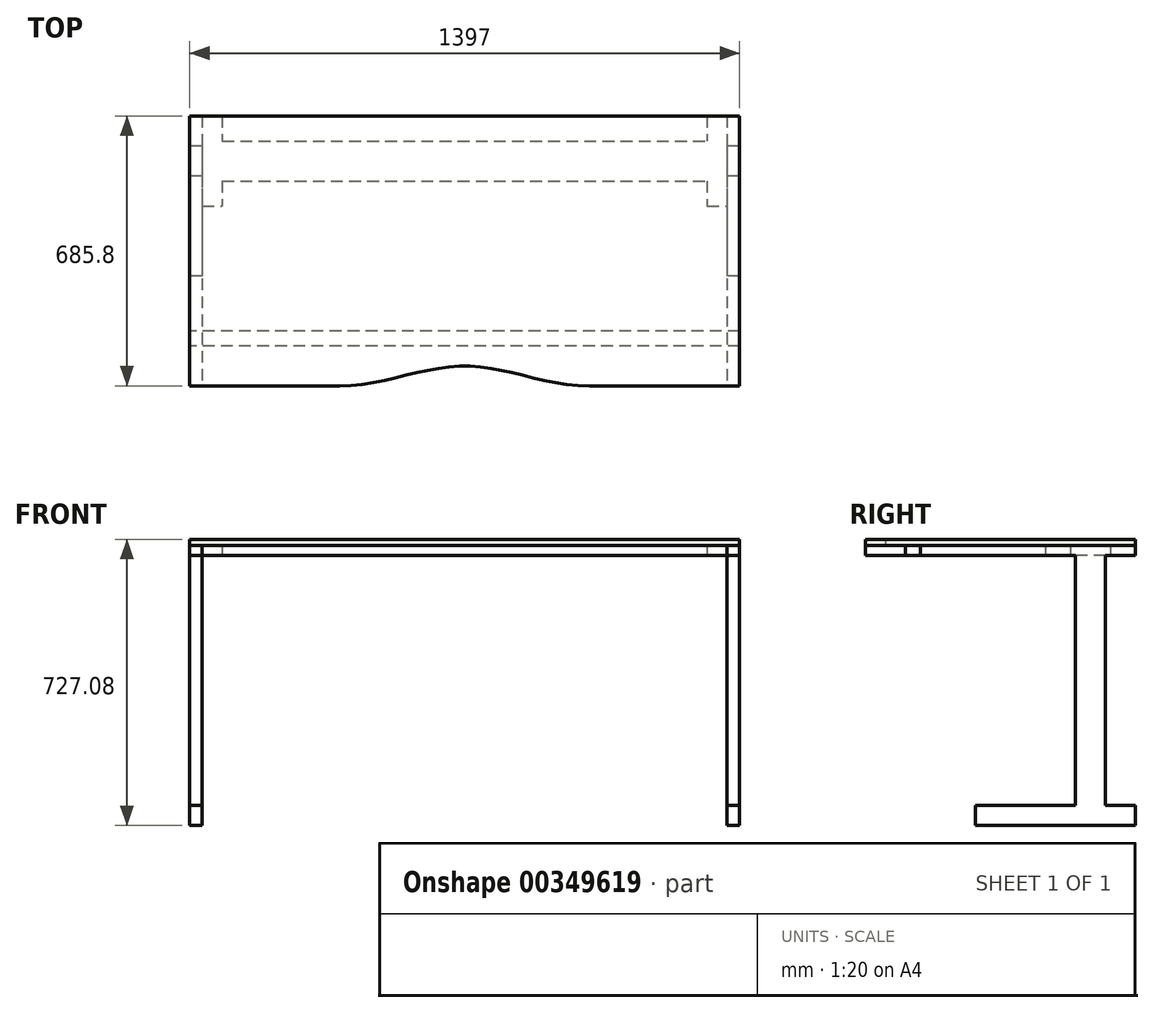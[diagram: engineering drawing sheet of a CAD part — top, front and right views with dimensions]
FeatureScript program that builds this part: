
annotation { "Feature Type Name" : "Feature", "Feature Type Description" : "" }
export const myFeature = defineFeature(function(context is Context, id is Id, definition is map)
    precondition{}
    {
        {
            var Q0;
            Q0=qCreatedBy(makeId("Top.planeOp"),FACE);
            var sketch = newSketch(context, id + "F0", { "sketchPlane" : qUnion([Q0])});
            skLineSegment(sketch, "E0.bottom", {"start": v(0, 0) * mm, "end": v(381, 0) * mm});
            skLineSegment(sketch, "E0.top", {"start": v(0, 685.8) * mm, "end": v(1397, 685.8) * mm});
            skLineSegment(sketch, "E0.left", {"start": v(0, 0) * mm, "end": v(0, 685.8) * mm});
            skLineSegment(sketch, "E0.right", {"start": v(1397, 0) * mm, "end": v(1397, 685.8) * mm});
            skPoint(sketch, "E1", {"position": v(1016, 0) * mm});
            skPoint(sketch, "E2", {"position": v(381, 0) * mm});
            skPoint(sketch, "E3", {"position": v(698.5, 50.8) * mm});
            skLineSegment(sketch, "E4.trimOffspring", {"start": v(1016, 0) * mm, "end": v(1397, 0) * mm});
            skFitSpline(sketch, "E5", {"points": [v(381, 0) * mm, v(698.5, 50.8) * mm, v(1016, 0) * mm], "startDerivative": vector(659.31, 0) * mm, "endDerivative": vector(699.63, 0) * mm});
            skSolve(sketch);
        }
        {
            var Q0;
            Q0 = qSketchRegion(id + "F0", true);
            extrude(context, id + "F1", {"entities" : qUnion([Q0]), "depth" : 15.88 * mm});
        }
        {
            var Q0;
            Q0=makeQuery(id+"F1.opExtrude","SWEPT_FACE",FACE,{"disambiguationData":[OSD([sQuery(id+"F0.wireOp",EDGE,"E0.left")])]});
            var sketch = newSketch(context, id + "F2", { "sketchPlane" : qUnion([Q0])});
            skPoint(sketch, "E6", {"position": v(-609.6, 0) * mm});
            skPoint(sketch, "E7", {"position": v(-533.4, 0) * mm});
            skLineSegment(sketch, "E8.bottom", {"start": v(-609.6, 0) * mm, "end": v(-533.4, 0) * mm});
            skLineSegment(sketch, "E8.top", {"start": v(-609.6, -711.2) * mm, "end": v(-533.4, -711.2) * mm});
            skLineSegment(sketch, "E8.left", {"start": v(-609.6, 0) * mm, "end": v(-609.6, -711.2) * mm});
            skLineSegment(sketch, "E8.right", {"start": v(-533.4, 0) * mm, "end": v(-533.4, -711.2) * mm});
            skLineSegment(sketch, "E9.bottom", {"start": v(-685.8, 0) * mm, "end": v(0, 0) * mm});
            skLineSegment(sketch, "E9.top", {"start": v(-685.8, -25.4) * mm, "end": v(0, -25.4) * mm});
            skLineSegment(sketch, "E9.left", {"start": v(-685.8, 0) * mm, "end": v(-685.8, -25.4) * mm});
            skLineSegment(sketch, "E9.right", {"start": v(0, 0) * mm, "end": v(0, -25.4) * mm});
            skSolve(sketch);
        }
        {
            var Q0;
            Q0 = qSketchRegion(id + "F2", true);
            extrude(context, id + "F3", {"entities" : qUnion([Q0]), "oppositeDirection" : true, "depth" : 1397 * mm});
        }
        {
            var Q0;
            Q0=makeQuery(id+"F3.opExtrude","SWEPT_FACE",FACE,{"disambiguationData":[OSD([sQuery(id+"F2.wireOp",EDGE,"E8.right")])]});
            var sketch = newSketch(context, id + "F4", { "sketchPlane" : qUnion([Q0])});
            skPoint(sketch, "E10", {"position": v(31.75, -711.2) * mm});
            skLineSegment(sketch, "E11.left", {"start": v(31.75, -711.2) * mm, "end": v(31.75, -711.2) * mm});
            skLineSegment(sketch, "E11.right", {"start": v(1365.25, -711.2) * mm, "end": v(1365.25, -711.2) * mm});
            skLineSegment(sketch, "E12.bottom", {"start": v(31.75, -711.2) * mm, "end": v(1365.25, -711.2) * mm});
            skLineSegment(sketch, "E12.top", {"start": v(31.75, -25.4) * mm, "end": v(1365.25, -25.4) * mm});
            skLineSegment(sketch, "E12.left", {"start": v(31.75, -711.2) * mm, "end": v(31.75, -25.4) * mm});
            skLineSegment(sketch, "E12.right", {"start": v(1365.25, -711.2) * mm, "end": v(1365.25, -25.4) * mm});
            skSolve(sketch);
        }
        {
            var Q0;
            Q0 = qSketchRegion(id + "F4", true);
            extrude(context, id + "F5", {"entities" : qUnion([Q0]), "operationType" : NewBodyOperationType.REMOVE, "oppositeDirection" : true, "depth" : 76.2 * mm});
        }
        {
            var Q0;
            Q0=makeQuery(id+"F3.boolean.opBoolean","MERGE",FACE,{"derivedFrom":[makeQuery(id+"F1.opExtrude","SWEPT_FACE",FACE,{"disambiguationData":[OSD([sQuery(id+"F0.wireOp",EDGE,"E0.bottom")])]}),makeQuery(id+"F1.opExtrude","SWEPT_FACE",FACE,{"disambiguationData":[OSD([sQuery(id+"F0.wireOp",EDGE,"E4.trimOffspring")])]}),makeQuery(id+"F3.opExtrude","SWEPT_FACE",FACE,{"disambiguationData":[OSD([sQuery(id+"F2.wireOp",EDGE,"E9.right")])]})]});
            var sketch = newSketch(context, id + "F6", { "sketchPlane" : qUnion([Q0])});
            skPoint(sketch, "E13", {"position": v(31.75, -25.4) * mm});
            skLineSegment(sketch, "E14.bottom", {"start": v(31.75, -25.4) * mm, "end": v(1365.25, -25.4) * mm});
            skLineSegment(sketch, "E14.top", {"start": v(31.75, 0) * mm, "end": v(1365.25, 0) * mm});
            skLineSegment(sketch, "E14.left", {"start": v(31.75, -25.4) * mm, "end": v(31.75, 0) * mm});
            skLineSegment(sketch, "E14.right", {"start": v(1365.25, -25.4) * mm, "end": v(1365.25, 0) * mm});
            skSolve(sketch);
        }
        {
            var Q0;
            Q0 = qSketchRegion(id + "F6", true);
            extrude(context, id + "F7", {"entities" : qUnion([Q0]), "operationType" : NewBodyOperationType.REMOVE, "oppositeDirection" : true, "depth" : 457.2 * mm});
        }
        {
            var Q0;
            Q0=makeQuery(id+"F3.opExtrude","CAP_FACE",FACE,{"disambiguationData":[OSD([sQuery(id+"F2.wireOp",EDGE,"E8.top"),sQuery(id+"F2.wireOp",EDGE,"E8.left"),sQuery(id+"F2.wireOp",EDGE,"E8.right"),sQuery(id+"F2.wireOp",EDGE,"E9.bottom"),sQuery(id+"F2.wireOp",EDGE,"E9.top"),sQuery(id+"F2.wireOp",EDGE,"E9.left"),sQuery(id+"F2.wireOp",EDGE,"E9.right")])],"isStart":true});
            var sketch = newSketch(context, id + "F8", { "sketchPlane" : qUnion([Q0])});
            skPoint(sketch, "E15", {"position": v(-685.8, -711.2) * mm});
            skPoint(sketch, "E16", {"position": v(-685.8, -660.4) * mm});
            skPoint(sketch, "E17", {"position": v(-279.4, -711.2) * mm});
            skPoint(sketch, "E18", {"position": v(-279.4, -660.4) * mm});
            skLineSegment(sketch, "E19.bottom", {"start": v(-685.8, -711.2) * mm, "end": v(-279.4, -711.2) * mm});
            skLineSegment(sketch, "E19.top", {"start": v(-685.8, -660.4) * mm, "end": v(-279.4, -660.4) * mm});
            skLineSegment(sketch, "E19.left", {"start": v(-685.8, -711.2) * mm, "end": v(-685.8, -660.4) * mm});
            skLineSegment(sketch, "E19.right", {"start": v(-279.4, -711.2) * mm, "end": v(-279.4, -660.4) * mm});
            skSolve(sketch);
        }
        {
            var Q0;
            Q0 = qSketchRegion(id + "F8", true);
            extrude(context, id + "F9", {"entities" : qUnion([Q0]), "operationType" : NewBodyOperationType.ADD, "oppositeDirection" : true, "depth" : 1397 * mm});
        }
        {
            var Q0;
            Q0=makeQuery(id+"F9.opExtrude","SWEPT_FACE",FACE,{"disambiguationData":[OSD([sQuery(id+"F8.wireOp",EDGE,"E19.right")])]});
            var sketch = newSketch(context, id + "F10", { "sketchPlane" : qUnion([Q0])});
            skPoint(sketch, "E20", {"position": v(31.75, -711.2) * mm});
            skPoint(sketch, "E21", {"position": v(31.75, -660.4) * mm});
            skLineSegment(sketch, "E22.bottom", {"start": v(31.75, -711.2) * mm, "end": v(1365.25, -711.2) * mm});
            skLineSegment(sketch, "E22.top", {"start": v(31.75, -660.4) * mm, "end": v(1365.25, -660.4) * mm});
            skLineSegment(sketch, "E22.left", {"start": v(31.75, -711.2) * mm, "end": v(31.75, -660.4) * mm});
            skLineSegment(sketch, "E22.right", {"start": v(1365.25, -711.2) * mm, "end": v(1365.25, -660.4) * mm});
            skSolve(sketch);
        }
        {
            var Q0;
            Q0 = qSketchRegion(id + "F10", true);
            extrude(context, id + "F11", {"entities" : qUnion([Q0]), "operationType" : NewBodyOperationType.REMOVE, "oppositeDirection" : true, "depth" : 457.2 * mm});
        }
        {
            var Q0;
            Q0=makeQuery(id+"F9.boolean.opBoolean","MERGE",FACE,{"derivedFrom":[makeQuery(id+"F3.opExtrude","CAP_FACE",FACE,{"disambiguationData":[OSD([sQuery(id+"F2.wireOp",EDGE,"E8.top"),sQuery(id+"F2.wireOp",EDGE,"E8.left"),sQuery(id+"F2.wireOp",EDGE,"E8.right"),sQuery(id+"F2.wireOp",EDGE,"E9.bottom"),sQuery(id+"F2.wireOp",EDGE,"E9.top"),sQuery(id+"F2.wireOp",EDGE,"E9.left"),sQuery(id+"F2.wireOp",EDGE,"E9.right")])],"isStart":true}),makeQuery(id+"F9.opExtrude","CAP_FACE",FACE,{"disambiguationData":[OSD([sQuery(id+"F8.wireOp",EDGE,"E19.bottom"),sQuery(id+"F8.wireOp",EDGE,"E19.top"),sQuery(id+"F8.wireOp",EDGE,"E19.left"),sQuery(id+"F8.wireOp",EDGE,"E19.right")])],"isStart":true})]});
            var sketch = newSketch(context, id + "F12", { "sketchPlane" : qUnion([Q0])});
            skPoint(sketch, "E23", {"position": v(-101.6, -25.4) * mm});
            skPoint(sketch, "E24", {"position": v(-139.7, -25.4) * mm});
            skLineSegment(sketch, "E25.bottom", {"start": v(-139.7, -25.4) * mm, "end": v(-101.6, -25.4) * mm});
            skLineSegment(sketch, "E25.top", {"start": v(-139.7, 0) * mm, "end": v(-101.6, 0) * mm});
            skLineSegment(sketch, "E25.left", {"start": v(-139.7, -25.4) * mm, "end": v(-139.7, 0) * mm});
            skLineSegment(sketch, "E25.right", {"start": v(-101.6, -25.4) * mm, "end": v(-101.6, 0) * mm});
            skSolve(sketch);
        }
        {
            var Q0;
            Q0 = qSketchRegion(id + "F12", true);
            extrude(context, id + "F13", {"entities" : qUnion([Q0]), "oppositeDirection" : true, "depth" : 1397 * mm});
        }
        {
            var Q0;
            {var subQ0=sQuery(id+"F2.wireOp",EDGE,"E9.top");Q0=makeQuery(id+"F5.boolean.opBoolean","MERGE",FACE,{"derivedFrom":[makeQuery(id+"F3.opExtrude","SWEPT_FACE",FACE,{"disambiguationData":[OSD([subQ0]),TDD([makeQuery(id+"F2.imprint","IMPRINT",EDGE,{"disambiguationData":[TD([[makeQuery(id+"F2.imprint","INTERSECT",VERTEX,{"derivedFrom":[subQ0,sQuery(id+"F2.wireOp",EDGE,"E9.left")]}),-1.0]])],"derivedFrom":subQ0})])]}),makeQuery(id+"F3.opExtrude","SWEPT_FACE",FACE,{"disambiguationData":[OSD([subQ0]),TDD([makeQuery(id+"F2.imprint","IMPRINT",EDGE,{"disambiguationData":[TD([[makeQuery(id+"F2.imprint","INTERSECT",VERTEX,{"derivedFrom":[subQ0,sQuery(id+"F2.wireOp",EDGE,"E9.right")]}),1.0]])],"derivedFrom":subQ0})])]}),makeQuery(id+"F5.opExtrude","SWEPT_FACE",FACE,{"disambiguationData":[OSD([sQuery(id+"F4.wireOp",EDGE,"E12.top")])]})]});}
            var sketch = newSketch(context, id + "F14", { "sketchPlane" : qUnion([Q0])});
            skPoint(sketch, "E26", {"position": v(82.55, -685.8) * mm});
            skPoint(sketch, "E27", {"position": v(1314.45, -685.8) * mm});
            skLineSegment(sketch, "E28.bottom", {"start": v(82.55, -685.8) * mm, "end": v(1314.45, -685.8) * mm});
            skLineSegment(sketch, "E28.top", {"start": v(82.55, -622.3) * mm, "end": v(1314.45, -622.3) * mm});
            skLineSegment(sketch, "E28.left", {"start": v(82.55, -685.8) * mm, "end": v(82.55, -622.3) * mm});
            skLineSegment(sketch, "E28.right", {"start": v(1314.45, -685.8) * mm, "end": v(1314.45, -622.3) * mm});
            skPoint(sketch, "E29", {"position": v(82.55, -520.7) * mm});
            skPoint(sketch, "E30", {"position": v(1314.45, -520.7) * mm});
            skPoint(sketch, "E31", {"position": v(1314.45, -457.2) * mm});
            skLineSegment(sketch, "E32.bottom", {"start": v(82.55, -520.7) * mm, "end": v(1314.45, -520.7) * mm});
            skLineSegment(sketch, "E32.top", {"start": v(82.55, -457.2) * mm, "end": v(1314.45, -457.2) * mm});
            skLineSegment(sketch, "E32.left", {"start": v(82.55, -520.7) * mm, "end": v(82.55, -457.2) * mm});
            skLineSegment(sketch, "E32.right", {"start": v(1314.45, -520.7) * mm, "end": v(1314.45, -457.2) * mm});
            skSolve(sketch);
        }
        {
            var Q0;
            Q0 = qSketchRegion(id + "F14", true);
            extrude(context, id + "F15", {"entities" : qUnion([Q0]), "operationType" : NewBodyOperationType.REMOVE, "oppositeDirection" : true, "depth" : 25.4 * mm});
        }
    });
